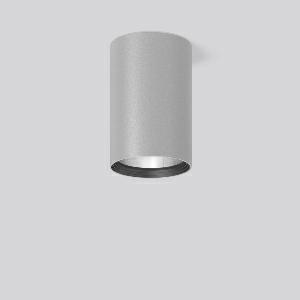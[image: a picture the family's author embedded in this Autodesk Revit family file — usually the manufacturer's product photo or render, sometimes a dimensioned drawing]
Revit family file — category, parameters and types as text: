
# Revit family: heledon_maxi_a_931223_004_1_f347
name_source: partatom
category: Lighting Fixtures
units: mm (PartAtom-declared; Revit-internal decimal feet)

## family parameters
Cut with Voids When Loaded = No
Host = Face
Light Source = No
Part Type = Normal
Room Calculation Point = No
Round Connector Dimension = Use Diameter
Shared = No

## types (1)
- HELEDON maxi A (1 x LED Modul 940, 4400 lm, 4000)
    Apparent Load = 35 VA
    Approval mark = CE
    CIE Flux Codes = 100 100 100 100 100
    Color Rendering = 92
    Color Temperature = 4000
    Default Elevation = 1800 mm
    Description = Series: HELEDON maxi
Cylindrical surface-mounted downlight. Housing: die-cast aluminium, powder-coated. Internal ceiling frame polycarbonate with bayonet mounting. Black plastic ring and recessed LED to prevent glare from the side. Optical assembly with reflector made of MIRO-Silver with 98% total light reflection for outstanding efficiency - can be changed without tools. Best colour rendering index Ra>90. Suitable for Ceiling mounting. Easy installation with a separate ceiling frame with bayonet mounting and plug connection. Driver integrated. Connected via plug-in connector. High quality converter without flickering and stroboscopic effect. The following accessories can be mounted without use of tools: interchangeable lenses, decorative glasses, honeycomb louvre, clear and frosted diffusers, white interchangeable plastic ring. 
Colour: silver
Diameter: 123 mm
Height: 183 mm
Lamp: LED
Socket: without socket
Colour temperature: 4000K
Colour rendering index (CRI): 92
System power: 35 W
Rated luminous flux: 4400 lm
Luminous efficiency: 126 lm/W
Control gear: Regulated power supply
Protection class: I
Type of protection: IP 20
    Height = 183 mm
    Lamp = 1 x LED Modul 940
    Lamp Light Flux = 4400 lm
    Lamp count = 1
    Length = 123 mm
    Lifetime = 50000 h
    Luminous efficacy = 126 lm/W
    Manufacturer = RZB
    ModVariant = No
    Model = 931223.004.1
    Mounting Place = Ceiling
    Mounting Type = Surface mounted
    Number of Poles = 1
    OnlyDefault = Yes
    Power Factor = 1
    Product Name = HELEDON maxi A
    Product group = Surface mounted downlights
    ProductGroupID = 302
    Protection Class = Protection class I
    Protection Degree = IP 20
    RLX_Detail_Level = 1
    RLX_Emergency_Light_Flux = 0 lm
    RLX_Emergency_Type = 0
    RLX_Emergency_Type_DB = No
    RlxData = <blob elided: 99017 chars, md5=837659e4>
    Socket = socket
    Standby Power = 0 W
    System Light Flux = 4400 lm
    System Power = 35 W
    Type Comments = Product without accessories
    Type Image = 931192.004.jpg
    URL = http://relux.com
    VarID = ---
    Voltage = 230 V
    Voltage Range = 220-240 V
    Weight = 0.00 kg
    Width = 0 mm  [stored 0 ft]

note: [stored X ft] marks values corroborated as IEEE doubles in the binary element streams (Revit-internal decimal feet)

## geometry (parser evidence)
native form markers: Blend x4, Sweep x10
no freeform markers — native parametric forms only
